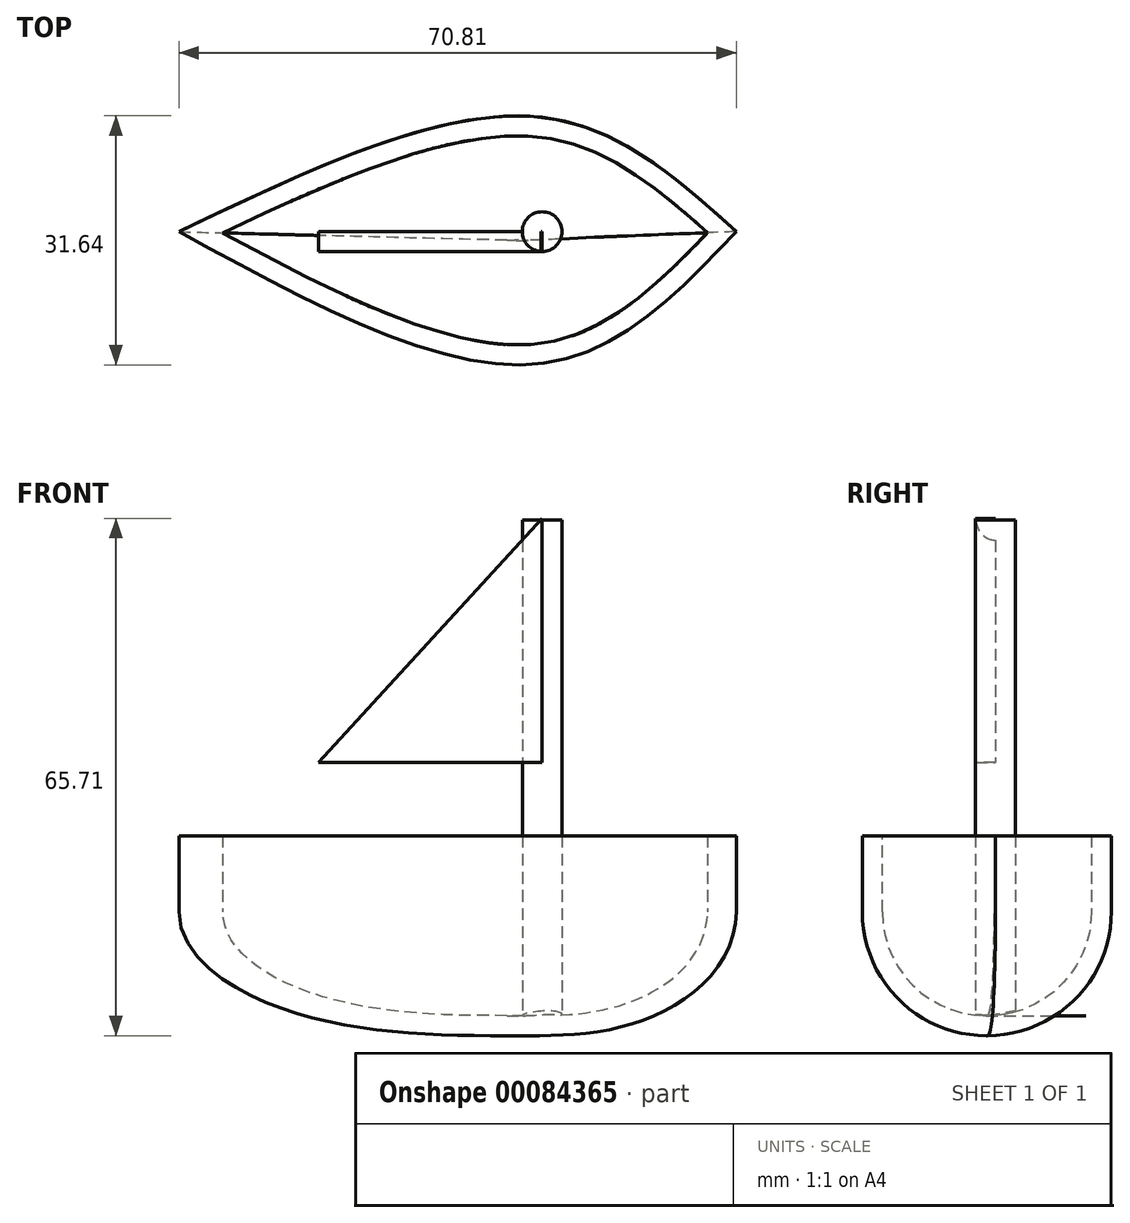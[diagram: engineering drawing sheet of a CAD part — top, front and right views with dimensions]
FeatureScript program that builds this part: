
annotation { "Feature Type Name" : "Feature", "Feature Type Description" : "" }
export const myFeature = defineFeature(function(context is Context, id is Id, definition is map)
    precondition{}
    {
        {
            var Q0;
            Q0=qCreatedBy(makeId("Top.planeOp"),FACE);
            var sketch = newSketch(context, id + "F0", { "sketchPlane" : qUnion([Q0])});
            skFitSpline(sketch, "E0", {"points": [v(24.66, 0) * mm, v(0, 14.54) * mm, v(-46.15, 0) * mm], "startDerivative": vector(-51.3, 46.3) * mm, "endDerivative": vector(-88.69, -42.44) * mm});
            skFitSpline(sketch, "E1", {"points": [v(24.66, 0) * mm, v(0, -16.75) * mm, v(-46.15, 0) * mm], "startDerivative": vector(-50.66, -53.14) * mm, "endDerivative": vector(-89.36, 48.92) * mm});
            skSolve(sketch);
        }
        {
            var Q0;
            Q0=makeQuery(id+"F0.imprint","IMPRINT",FACE,{"disambiguationData":[TD([[makeQuery(id+"F0.imprint","IMPRINT",EDGE,{"derivedFrom":sQuery(id+"F0.wireOp",EDGE,"E0")}),1.0]])]});
            extrude(context, id + "F1", {"entities" : qUnion([Q0]), "depth" : 25.4 * mm});
        }
        {
            var Q0;
            Q0=makeQuery(id+"F1.opExtrude","CAP_EDGE",EDGE,{"disambiguationData":[OSD([sQuery(id+"F0.wireOp",EDGE,"E1")])],"isStart":true});
            var Q1;
            Q1=makeQuery(id+"F1.opExtrude","CAP_EDGE",EDGE,{"disambiguationData":[OSD([sQuery(id+"F0.wireOp",EDGE,"E0")])],"isStart":true});
            fillet(context, id + "F2", {"entities" : qUnion([Q0, Q1]), "radius" : 15.75 * mm, "tangentPropagation" : true, "allowEdgeOverflow" : false});
        }
        {
            var Q0;
            Q0=makeQuery(id+"F1.opExtrude","CAP_FACE",FACE,{"disambiguationData":[OSD([sQuery(id+"F0.wireOp",EDGE,"E0"),sQuery(id+"F0.wireOp",EDGE,"E1")])],"isStart":false});
            shell(context, id + "F3", {"entities" : qUnion([Q0]), "thickness" : 2.54 * mm});
        }
        {
            var Q0;
            Q0=qCreatedBy(makeId("Top.planeOp"),FACE);
            cPlane(context, id + "F4", {"entities" : qUnion([Q0]), "cplaneType" : CPlaneType.OFFSET, "offset" : 2.03 * mm, "width" : 152.4 * mm, "height" : 152.4 * mm});
        }
        {
            var Q0;
            Q0=qCreatedBy(id+"F4.planeOp",FACE);
            var sketch = newSketch(context, id + "F5", { "sketchPlane" : qUnion([Q0])});
            skCircle(sketch, "E2", {"center": v(0, 0) * mm, "radius": 2.53 * mm});
            skSolve(sketch);
        }
        {
            var Q0;
            Q0 = qSketchRegion(id + "F5", true);
            extrude(context, id + "F6", {"entities" : qUnion([Q0]), "operationType" : NewBodyOperationType.ADD, "depth" : 63.5 * mm});
        }
        {
            var Q0;
            Q0=qCreatedBy(makeId("Front.planeOp"),FACE);
            var sketch = newSketch(context, id + "F7", { "sketchPlane" : qUnion([Q0])});
            skLineSegment(sketch, "E3", {"start": v(0, 65.7) * mm, "end": v(-28.38, 34.72) * mm});
            skLineSegment(sketch, "E4", {"start": v(-28.38, 34.72) * mm, "end": v(0, 34.72) * mm});
            skLineSegment(sketch, "E5", {"start": v(0, 34.72) * mm, "end": v(0, 65.7) * mm});
            skSolve(sketch);
        }
        {
            var Q0;
            Q0=makeQuery(id+"F7.imprint","IMPRINT",FACE,{"disambiguationData":[TD([[makeQuery(id+"F7.imprint","IMPRINT",EDGE,{"derivedFrom":sQuery(id+"F7.wireOp",EDGE,"E3")}),1.0]])]});
            extrude(context, id + "F8", {"entities" : qUnion([Q0]), "operationType" : NewBodyOperationType.ADD, "depth" : 2.54 * mm});
        }
    });
